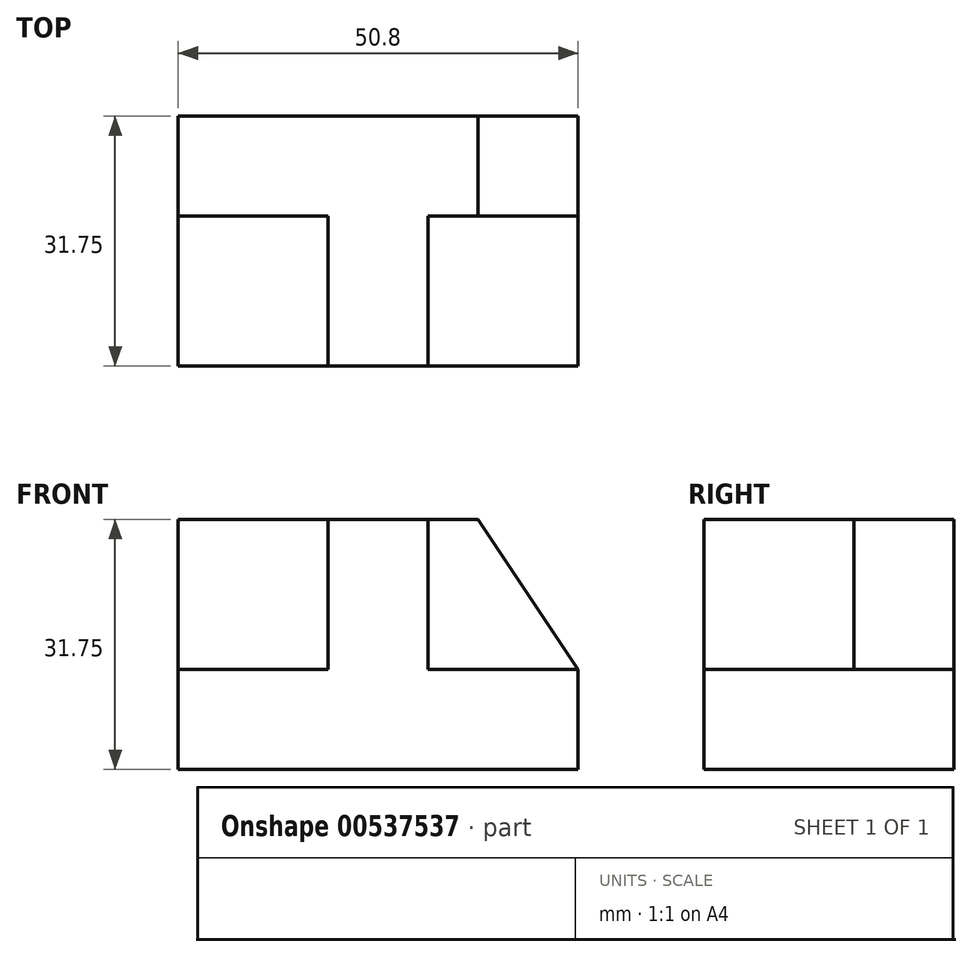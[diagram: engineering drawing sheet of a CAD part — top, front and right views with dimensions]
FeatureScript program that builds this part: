
annotation { "Feature Type Name" : "Feature", "Feature Type Description" : "" }
export const myFeature = defineFeature(function(context is Context, id is Id, definition is map)
    precondition{}
    {
        {
            var Q0;
            Q0=qCreatedBy(makeId("Front.planeOp"),FACE);
            var sketch = newSketch(context, id + "F0", { "sketchPlane" : qUnion([Q0])});
            skLineSegment(sketch, "E0", {"start": v(0, 0) * mm, "end": v(0, 31.75) * mm});
            skLineSegment(sketch, "E1", {"start": v(0, 31.75) * mm, "end": v(-50.8, 31.75) * mm});
            skLineSegment(sketch, "E2", {"start": v(-50.8, 31.75) * mm, "end": v(-50.8, 0) * mm});
            skLineSegment(sketch, "E3", {"start": v(-50.8, 0) * mm, "end": v(0, 0) * mm});
            skSolve(sketch);
        }
        {
            var Q0;
            Q0 = qSketchRegion(id + "F0", true);
            extrude(context, id + "F1", {"entities" : qUnion([Q0]), "depth" : 31.75 * mm, "offsetDistance" : 25.4 * mm});
        }
        {
            var Q0;
            Q0=makeQuery(id+"F1.opExtrude","SWEPT_FACE",FACE,{"disambiguationData":[OSD([sQuery(id+"F0.wireOp",EDGE,"E1")])]});
            var sketch = newSketch(context, id + "F2", { "sketchPlane" : qUnion([Q0])});
            skLineSegment(sketch, "E4", {"start": v(0, -31.75) * mm, "end": v(-19.05, -31.75) * mm});
            skLineSegment(sketch, "E5", {"start": v(-19.05, -31.75) * mm, "end": v(-19.05, -12.7) * mm});
            skLineSegment(sketch, "E6", {"start": v(-19.05, -12.7) * mm, "end": v(0, -12.7) * mm});
            skLineSegment(sketch, "E7", {"start": v(0, -12.7) * mm, "end": v(0, -31.75) * mm});
            skSolve(sketch);
        }
        {
            var Q0;
            Q0=makeQuery(id+"F2.imprint","IMPRINT",FACE,{"disambiguationData":[TD([[makeQuery(id+"F2.imprint","IMPRINT",EDGE,{"derivedFrom":sQuery(id+"F2.wireOp",EDGE,"E4")}),-1.0]])]});
            extrude(context, id + "F3", {"entities" : qUnion([Q0]), "operationType" : NewBodyOperationType.REMOVE, "oppositeDirection" : true, "depth" : 19.05 * mm, "offsetDistance" : 25.4 * mm});
        }
        {
            var Q0;
            Q0=makeQuery(id+"F1.opExtrude","CAP_FACE",FACE,{"disambiguationData":[OSD([sQuery(id+"F0.wireOp",EDGE,"E0"),sQuery(id+"F0.wireOp",EDGE,"E1"),sQuery(id+"F0.wireOp",EDGE,"E2"),sQuery(id+"F0.wireOp",EDGE,"E3")])],"isStart":false});
            var sketch = newSketch(context, id + "F4", { "sketchPlane" : qUnion([Q0])});
            skLineSegment(sketch, "E8", {"start": v(-50.8, 12.7) * mm, "end": v(-31.75, 12.7) * mm});
            skLineSegment(sketch, "E9", {"start": v(-31.75, 12.7) * mm, "end": v(-31.75, 31.75) * mm});
            skLineSegment(sketch, "E10", {"start": v(-31.75, 31.75) * mm, "end": v(-50.8, 31.75) * mm});
            skLineSegment(sketch, "E11", {"start": v(-50.8, 31.75) * mm, "end": v(-50.8, 12.7) * mm});
            skSolve(sketch);
        }
        {
            var Q0;
            Q0=makeQuery(id+"F4.imprint","IMPRINT",FACE,{"disambiguationData":[TD([[makeQuery(id+"F4.imprint","IMPRINT",EDGE,{"derivedFrom":sQuery(id+"F4.wireOp",EDGE,"E8")}),1.0]])]});
            extrude(context, id + "F5", {"entities" : qUnion([Q0]), "operationType" : NewBodyOperationType.REMOVE, "oppositeDirection" : true, "depth" : 19.05 * mm, "offsetDistance" : 25.4 * mm});
        }
        {
            var Q0;
            Q0=makeQuery(id+"F3.boolean.opBoolean","COPY",FACE,{"derivedFrom":makeQuery(id+"F3.opExtrude","SWEPT_FACE",FACE,{"disambiguationData":[OSD([sQuery(id+"F2.wireOp",EDGE,"E6")])]})});
            var sketch = newSketch(context, id + "F6", { "sketchPlane" : qUnion([Q0])});
            skLineSegment(sketch, "E12", {"start": v(-12.7, 31.75) * mm, "end": v(0, 12.7) * mm});
            skLineSegment(sketch, "E13", {"start": v(0, 12.7) * mm, "end": v(0, 31.75) * mm});
            skLineSegment(sketch, "E14", {"start": v(0, 31.75) * mm, "end": v(-12.7, 31.75) * mm});
            skSolve(sketch);
        }
        {
            var Q0;
            Q0=makeQuery(id+"F6.imprint","IMPRINT",FACE,{"disambiguationData":[TD([[makeQuery(id+"F6.imprint","IMPRINT",EDGE,{"derivedFrom":sQuery(id+"F6.wireOp",EDGE,"E12")}),1.0]])]});
            extrude(context, id + "F7", {"entities" : qUnion([Q0]), "operationType" : NewBodyOperationType.REMOVE, "oppositeDirection" : true, "depth" : 12.7 * mm, "offsetDistance" : 25.4 * mm});
        }
    });
